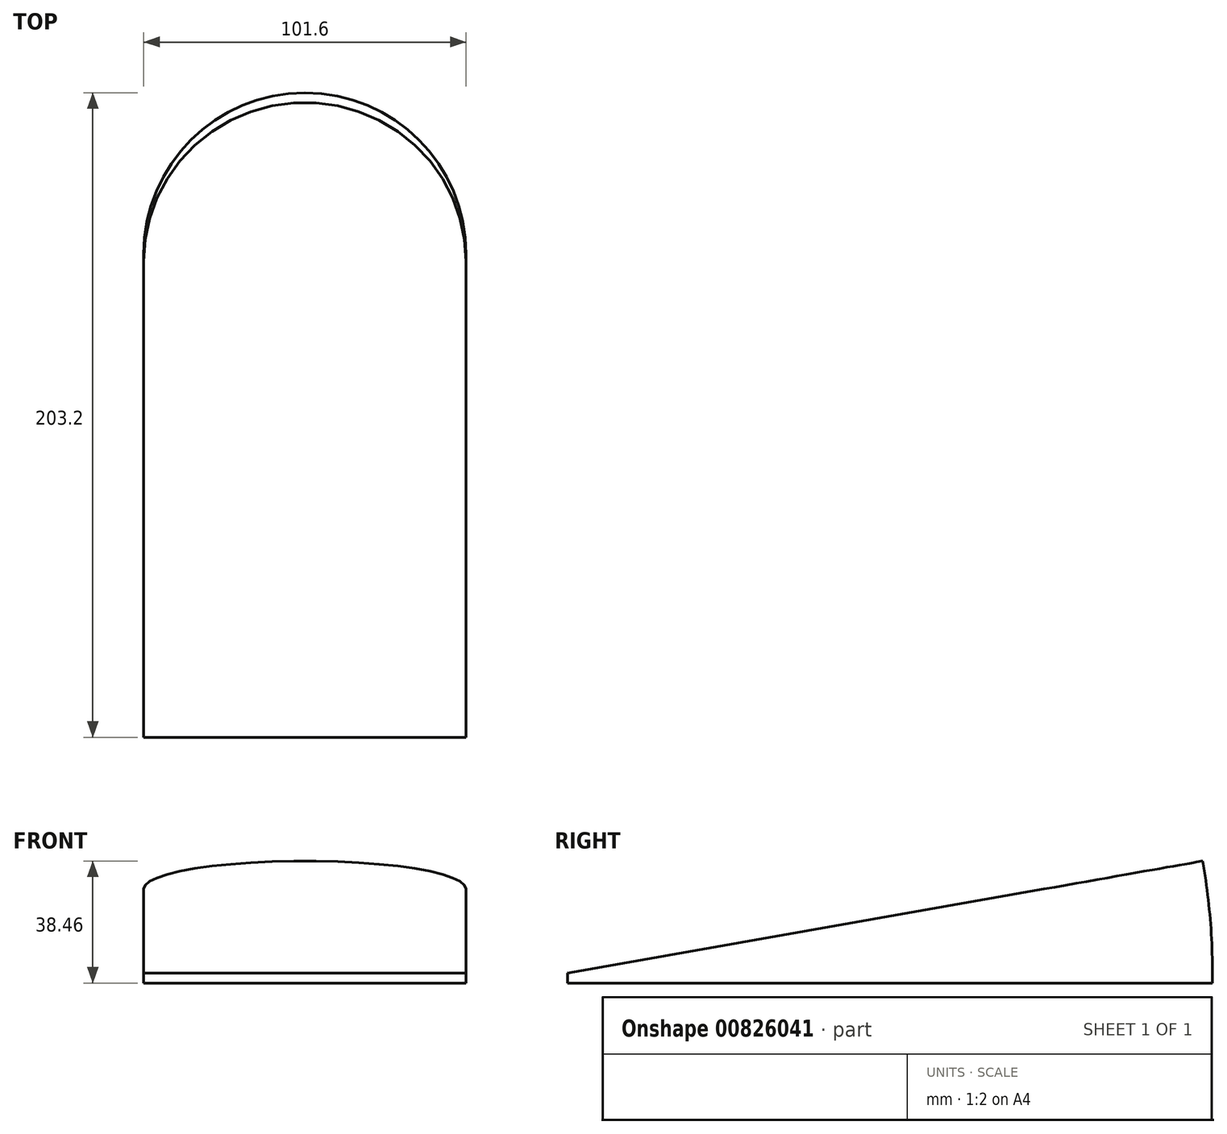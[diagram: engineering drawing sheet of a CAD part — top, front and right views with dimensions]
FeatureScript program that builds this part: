
annotation { "Feature Type Name" : "Feature", "Feature Type Description" : "" }
export const myFeature = defineFeature(function(context is Context, id is Id, definition is map)
    precondition{}
    {
        {
            var Q0;
            Q0=qCreatedBy(makeId("Top.planeOp"),FACE);
            var sketch = newSketch(context, id + "F0", { "sketchPlane" : qUnion([Q0])});
            skLineSegment(sketch, "E0.bottom", {"start": v(50.8, -76.2) * mm, "end": v(-50.8, -76.2) * mm});
            skLineSegment(sketch, "E0.top", {"start": v(50.8, 76.2) * mm, "end": v(-50.8, 76.2) * mm});
            skLineSegment(sketch, "E0.left", {"start": v(50.8, -76.2) * mm, "end": v(50.8, 76.2) * mm});
            skLineSegment(sketch, "E0.right", {"start": v(-50.8, -76.2) * mm, "end": v(-50.8, 76.2) * mm});
            skPoint(sketch, "E0.middle", {"position": v(0, 0) * mm});
            skCircle(sketch, "E1", {"center": v(0, 76.2) * mm, "radius": 50.8 * mm});
            skSolve(sketch);
        }
        {
            var Q0;
            {var subQ0=sQuery(id+"F0.wireOp",EDGE,"E0.top");Q0=makeQuery(id+"F0.imprint","IMPRINT",FACE,{"disambiguationData":[TD([[makeQuery(id+"F0.imprint","IMPRINT",EDGE,{"derivedFrom":subQ0}),-1.0]])]});}
            var Q1;
            Q1=makeQuery(id+"F0.imprint","IMPRINT",FACE,{"disambiguationData":[TD([[makeQuery(id+"F0.imprint","IMPRINT",EDGE,{"derivedFrom":sQuery(id+"F0.wireOp",EDGE,"E0.bottom")}),-1.0]])]});
            var Q2;
            {var subQ0=sQuery(id+"F0.wireOp",EDGE,"E0.top");Q2=makeQuery(id+"F0.imprint","IMPRINT",FACE,{"disambiguationData":[TD([[makeQuery(id+"F0.imprint","IMPRINT",EDGE,{"derivedFrom":subQ0}),1.0]])]});}
            extrude(context, id + "F1", {"entities" : qUnion([Q0, Q1, Q2]), "depth" : 3.17 * mm, "offsetDistance" : 25.4 * mm});
        }
        {
            var Q0;
            Q0=makeQuery(id+"F1.opExtrude","CAP_FACE",FACE,{"disambiguationData":[OSD([sQuery(id+"F0.wireOp",EDGE,"E0.bottom"),sQuery(id+"F0.wireOp",EDGE,"E0.left"),sQuery(id+"F0.wireOp",EDGE,"E0.right"),sQuery(id+"F0.wireOp",EDGE,"E1")])],"isStart":false});
            var Q1;
            Q1=makeQuery(id+"F1.opExtrude","CAP_EDGE",EDGE,{"disambiguationData":[OSD([sQuery(id+"F0.wireOp",EDGE,"E0.bottom")])],"isStart":false});
            revolve(context, id + "F2", {"operationType" : NewBodyOperationType.ADD, "surfaceOperationType" : NewSurfaceOperationType.NEW, "entities" : qUnion([Q0]), "axis" : qUnion([Q1]), "revolveType" : RevolveType.ONE_DIRECTION, "oppositeDirection" : true, "angle" : 10 * degree});
        }
    });
